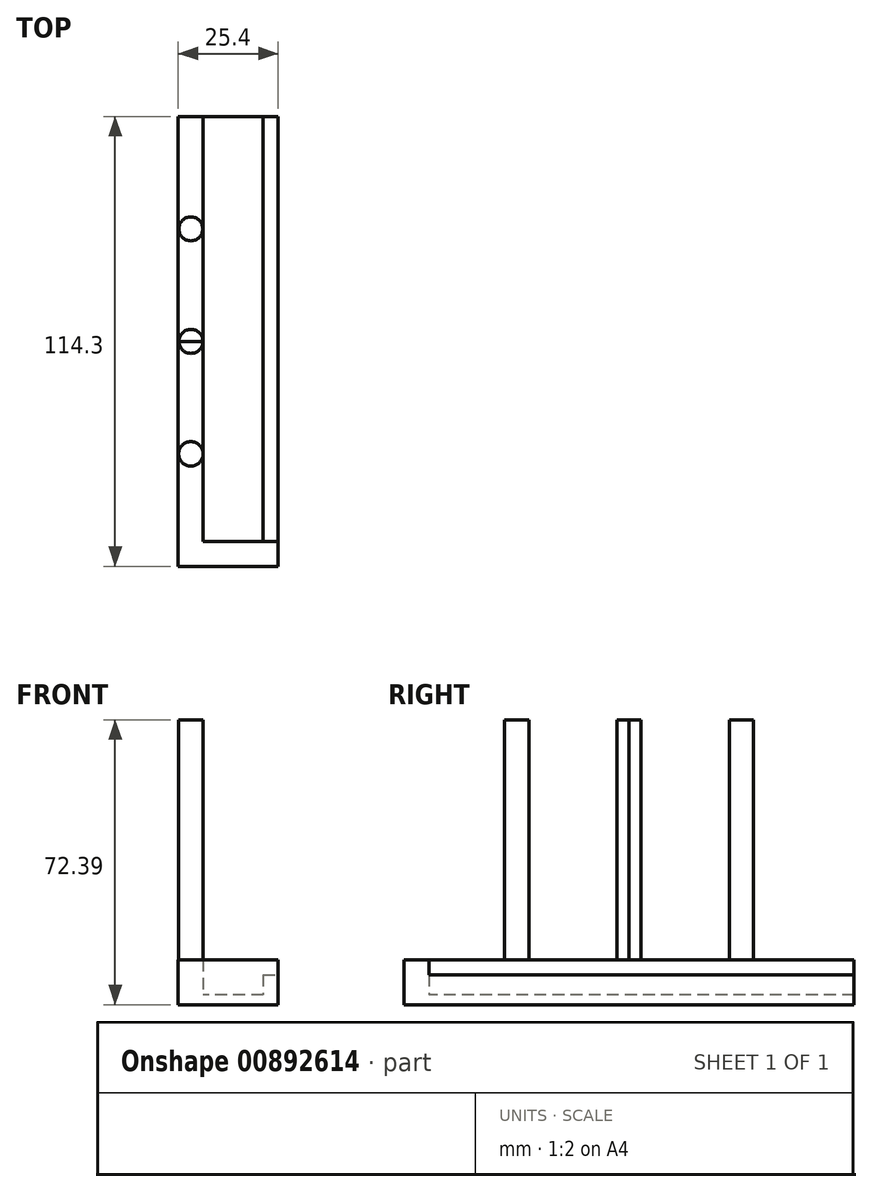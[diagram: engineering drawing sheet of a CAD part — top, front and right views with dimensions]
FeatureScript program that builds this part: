
annotation { "Feature Type Name" : "Feature", "Feature Type Description" : "" }
export const myFeature = defineFeature(function(context is Context, id is Id, definition is map)
    precondition{}
    {
        {
            var Q0;
            Q0=qCreatedBy(makeId("Top.planeOp"),FACE);
            var sketch = newSketch(context, id + "F0", { "sketchPlane" : qUnion([Q0])});
            skLineSegment(sketch, "E0.bottom", {"start": v(5.72, -57.15) * mm, "end": v(-5.71, -57.15) * mm});
            skLineSegment(sketch, "E0.top", {"start": v(5.71, 57.15) * mm, "end": v(3.17, 57.15) * mm});
            skLineSegment(sketch, "E0.left", {"start": v(5.72, -57.15) * mm, "end": v(5.71, 57.15) * mm});
            skLineSegment(sketch, "E0.right", {"start": v(-5.71, -57.15) * mm, "end": v(-5.72, 57.15) * mm});
            skPoint(sketch, "E0.middle", {"position": v(0, 0) * mm});
            skLineSegment(sketch, "E1", {"start": v(3.17, 57.15) * mm, "end": v(3.18, -57.15) * mm});
            skLineSegment(sketch, "E2", {"start": v(3.17, 57.15) * mm, "end": v(-5.72, 57.15) * mm});
            skSolve(sketch);
        }
        {
            var Q0;
            {var subQ0=sQuery(id+"F0.wireOp",EDGE,"E0.right");Q0=makeQuery(id+"F0.imprint","IMPRINT",FACE,{"disambiguationData":[TD([[makeQuery(id+"F0.imprint","IMPRINT",EDGE,{"derivedFrom":subQ0}),-1.0]])]});}
            extrude(context, id + "F1", {"entities" : qUnion([Q0]), "depth" : 6.35 * mm, "offsetDistance" : 25.4 * mm});
        }
        {
            var Q0;
            Q0=makeQuery(id+"F0.imprint","IMPRINT",FACE,{"disambiguationData":[TD([[makeQuery(id+"F0.imprint","IMPRINT",EDGE,{"derivedFrom":sQuery(id+"F0.wireOp",EDGE,"E0.top")}),1.0]])]});
            extrude(context, id + "F2", {"entities" : qUnion([Q0]), "operationType" : NewBodyOperationType.ADD, "depth" : 25.4 * mm, "offsetDistance" : 25.4 * mm});
        }
        {
            var Q0;
            Q0=makeQuery(id+"F2.opExtrude","SWEPT_FACE",FACE,{"disambiguationData":[OSD([sQuery(id+"F0.wireOp",EDGE,"E1")])]});
            var sketch = newSketch(context, id + "F3", { "sketchPlane" : qUnion([Q0])});
            skLineSegment(sketch, "E3.bottom", {"start": v(-57.15, 25.4) * mm, "end": v(57.15, 25.4) * mm});
            skLineSegment(sketch, "E3.top", {"start": v(-57.15, 21.6) * mm, "end": v(57.15, 21.6) * mm});
            skLineSegment(sketch, "E3.left", {"start": v(-57.15, 25.4) * mm, "end": v(-57.15, 21.6) * mm});
            skLineSegment(sketch, "E3.right", {"start": v(57.15, 25.4) * mm, "end": v(57.15, 21.6) * mm});
            skSolve(sketch);
        }
        {
            var Q0;
            Q0=makeQuery(id+"F3.imprint","IMPRINT",FACE,{"disambiguationData":[TD([[makeQuery(id+"F3.imprint","IMPRINT",EDGE,{"derivedFrom":sQuery(id+"F3.wireOp",EDGE,"E3.bottom")}),-1.0]])]});
            extrude(context, id + "F4", {"entities" : qUnion([Q0]), "operationType" : NewBodyOperationType.ADD, "depth" : 5.08 * mm, "offsetDistance" : 25.4 * mm});
        }
        {
            var Q0;
            Q0=makeQuery(id+"F1.opExtrude","SWEPT_FACE",FACE,{"disambiguationData":[OSD([sQuery(id+"F0.wireOp",EDGE,"E0.right")])]});
            var sketch = newSketch(context, id + "F5", { "sketchPlane" : qUnion([Q0])});
            skLineSegment(sketch, "E4", {"start": v(-57.15, 0) * mm, "end": v(57.15, 0) * mm});
            skLineSegment(sketch, "E5", {"start": v(57.15, 6.35) * mm, "end": v(-57.15, 6.35) * mm});
            skLineSegment(sketch, "E6", {"start": v(-57.15, 6.35) * mm, "end": v(-57.15, 0) * mm});
            skLineSegment(sketch, "E7", {"start": v(0, 0) * mm, "end": v(0, 6.35) * mm});
            skLineSegment(sketch, "E8", {"start": v(-44.43, 6.35) * mm, "end": v(-57.13, 6.35) * mm});
            skLineSegment(sketch, "E9", {"start": v(0.02, 0) * mm, "end": v(0.02, 0.14) * mm});
            skPoint(sketch, "E10", {"position": v(0.02, 0) * mm});
            skLineSegment(sketch, "E11", {"start": v(0.02, 0.14) * mm, "end": v(0.02, 6.35) * mm});
            skLineSegment(sketch, "E12", {"start": v(-57.13, 0) * mm, "end": v(-28.56, 0.07) * mm});
            skLineSegment(sketch, "E13", {"start": v(-28.56, 0.07) * mm, "end": v(0.02, 0.14) * mm});
            skLineSegment(sketch, "E14", {"start": v(-28.56, 0.07) * mm, "end": v(-28.57, 6.35) * mm});
            skLineSegment(sketch, "E15", {"start": v(0.02, 0.14) * mm, "end": v(28.6, 0.07) * mm});
            skLineSegment(sketch, "E16", {"start": v(28.6, 0.07) * mm, "end": v(28.6, 6.35) * mm});
            skPoint(sketch, "E17", {"position": v(28.6, 0.07) * mm});
            skLineSegment(sketch, "E18", {"start": v(28.6, 0.07) * mm, "end": v(57.17, 0) * mm});
            skCircle(sketch, "E19", {"center": v(-28.57, 3.2) * mm, "radius": 3.05 * mm});
            skCircle(sketch, "E20", {"center": v(28.6, 3.2) * mm, "radius": 3.11 * mm});
            skCircle(sketch, "E21", {"center": v(0.02, 3.24) * mm, "radius": 3.05 * mm});
            skSolve(sketch);
        }
        {
            var Q0;
            {var subQ0=sQuery(id+"F5.wireOp",EDGE,"E19");var subQ1=sQuery(id+"F5.wireOp",EDGE,"E14");var subQ2=makeQuery(id+"F5.imprint","INTERSECT",VERTEX,{"disambiguationData":[OD(0.0)],"derivedFrom":[subQ1,subQ0]});Q0=makeQuery(id+"F5.imprint","IMPRINT",FACE,{"disambiguationData":[TD([[makeQuery(id+"F5.imprint","IMPRINT",EDGE,{"disambiguationData":[TD([[subQ2,-1.0]])],"derivedFrom":subQ1}),1.0]])]});}
            var Q1;
            {var subQ0=sQuery(id+"F5.wireOp",EDGE,"E19");var subQ1=sQuery(id+"F5.wireOp",EDGE,"E14");var subQ2=makeQuery(id+"F5.imprint","INTERSECT",VERTEX,{"disambiguationData":[OD(0.0)],"derivedFrom":[subQ1,subQ0]});Q1=makeQuery(id+"F5.imprint","IMPRINT",FACE,{"disambiguationData":[TD([[makeQuery(id+"F5.imprint","IMPRINT",EDGE,{"disambiguationData":[TD([[subQ2,-1.0]])],"derivedFrom":subQ1}),-1.0]])]});}
            var Q2;
            {var subQ0=sQuery(id+"F5.wireOp",EDGE,"E20");var subQ1=sQuery(id+"F5.wireOp",EDGE,"E16");var subQ2=makeQuery(id+"F5.imprint","INTERSECT",VERTEX,{"disambiguationData":[OD(0.0)],"derivedFrom":[subQ1,subQ0]});Q2=makeQuery(id+"F5.imprint","IMPRINT",FACE,{"disambiguationData":[TD([[makeQuery(id+"F5.imprint","IMPRINT",EDGE,{"disambiguationData":[TD([[subQ2,-1.0]])],"derivedFrom":subQ1}),1.0]])]});}
            var Q3;
            {var subQ0=sQuery(id+"F5.wireOp",EDGE,"E20");var subQ1=sQuery(id+"F5.wireOp",EDGE,"E16");var subQ2=makeQuery(id+"F5.imprint","INTERSECT",VERTEX,{"disambiguationData":[OD(0.0)],"derivedFrom":[subQ1,subQ0]});Q3=makeQuery(id+"F5.imprint","IMPRINT",FACE,{"disambiguationData":[TD([[makeQuery(id+"F5.imprint","IMPRINT",EDGE,{"disambiguationData":[TD([[subQ2,-1.0]])],"derivedFrom":subQ1}),-1.0]])]});}
            var Q4;
            {var subQ0=sQuery(id+"F5.wireOp",EDGE,"E21");var subQ1=sQuery(id+"F5.wireOp",EDGE,"E7");var subQ2=makeQuery(id+"F5.imprint","INTERSECT",VERTEX,{"disambiguationData":[OD(0.0)],"derivedFrom":[subQ1,subQ0]});Q4=makeQuery(id+"F5.imprint","IMPRINT",FACE,{"disambiguationData":[TD([[makeQuery(id+"F5.imprint","IMPRINT",EDGE,{"disambiguationData":[TD([[subQ2,-1.0]])],"derivedFrom":subQ1}),1.0]])]});}
            var Q5;
            {var subQ0=sQuery(id+"F5.wireOp",EDGE,"E21");var subQ1=sQuery(id+"F5.wireOp",EDGE,"E11");var subQ2=makeQuery(id+"F5.imprint","INTERSECT",VERTEX,{"disambiguationData":[OD(0.0)],"derivedFrom":[subQ1,subQ0]});Q5=makeQuery(id+"F5.imprint","IMPRINT",FACE,{"disambiguationData":[TD([[makeQuery(id+"F5.imprint","IMPRINT",EDGE,{"disambiguationData":[TD([[subQ2,-1.0]])],"derivedFrom":subQ1}),-1.0]])]});}
            extrude(context, id + "F6", {"entities" : qUnion([Q0, Q1, Q2, Q3, Q4, Q5]), "operationType" : NewBodyOperationType.ADD, "depth" : 60.96 * mm, "offsetDistance" : 25.4 * mm});
        }
        {
            var Q0;
            {var subQ0=sQuery(id+"F0.wireOp",EDGE,"E0.bottom");Q0=makeQuery(id+"F4.boolean.opBoolean","MERGE",FACE,{"derivedFrom":[makeQuery(id+"F2.boolean.opBoolean","MERGE",FACE,{"derivedFrom":[makeQuery(id+"F1.opExtrude","SWEPT_FACE",FACE,{"disambiguationData":[OSD([subQ0])]}),makeQuery(id+"F2.opExtrude","SWEPT_FACE",FACE,{"disambiguationData":[OSD([subQ0])]})]}),makeQuery(id+"F4.opExtrude","SWEPT_FACE",FACE,{"disambiguationData":[OSD([sQuery(id+"F3.wireOp",EDGE,"E3.right")])]})]});}
            var sketch = newSketch(context, id + "F7", { "sketchPlane" : qUnion([Q0])});
            skLineSegment(sketch, "E22", {"start": v(5.72, 25.4) * mm, "end": v(5.72, 0) * mm});
            skLineSegment(sketch, "E23", {"start": v(5.72, 0) * mm, "end": v(-5.71, 0) * mm});
            skLineSegment(sketch, "E24", {"start": v(-5.71, 0) * mm, "end": v(-5.71, 25.4) * mm});
            skLineSegment(sketch, "E25", {"start": v(-5.71, 25.4) * mm, "end": v(5.72, 25.4) * mm});
            skSolve(sketch);
        }
        {
            var Q0;
            Q0 = qSketchRegion(id + "F7", true);
            extrude(context, id + "F8", {"entities" : qUnion([Q0]), "operationType" : NewBodyOperationType.ADD, "depth" : -6.35 * mm, "offsetDistance" : 25.4 * mm});
        }
        {
            var Q0;
            Q0=makeQuery(id+"F1.opExtrude","SWEPT_BODY",BODY,{"disambiguationData":[OSD([sQuery(id+"F0.wireOp",EDGE,"E0.bottom"),sQuery(id+"F0.wireOp",EDGE,"E0.right"),sQuery(id+"F0.wireOp",EDGE,"E1"),sQuery(id+"F0.wireOp",EDGE,"E2")])]});
            var Q1;
            Q1=sQuery(id+"F0.wireOp",EDGE,"E1");
            transform(context, id + "F9", {"entities" : qUnion([Q0]), "transformType" : TransformType.ROTATION, "transformAxis" : qUnion([Q1]), "angle" : 270 * degree, "makeCopy" : false});
        }
    });
